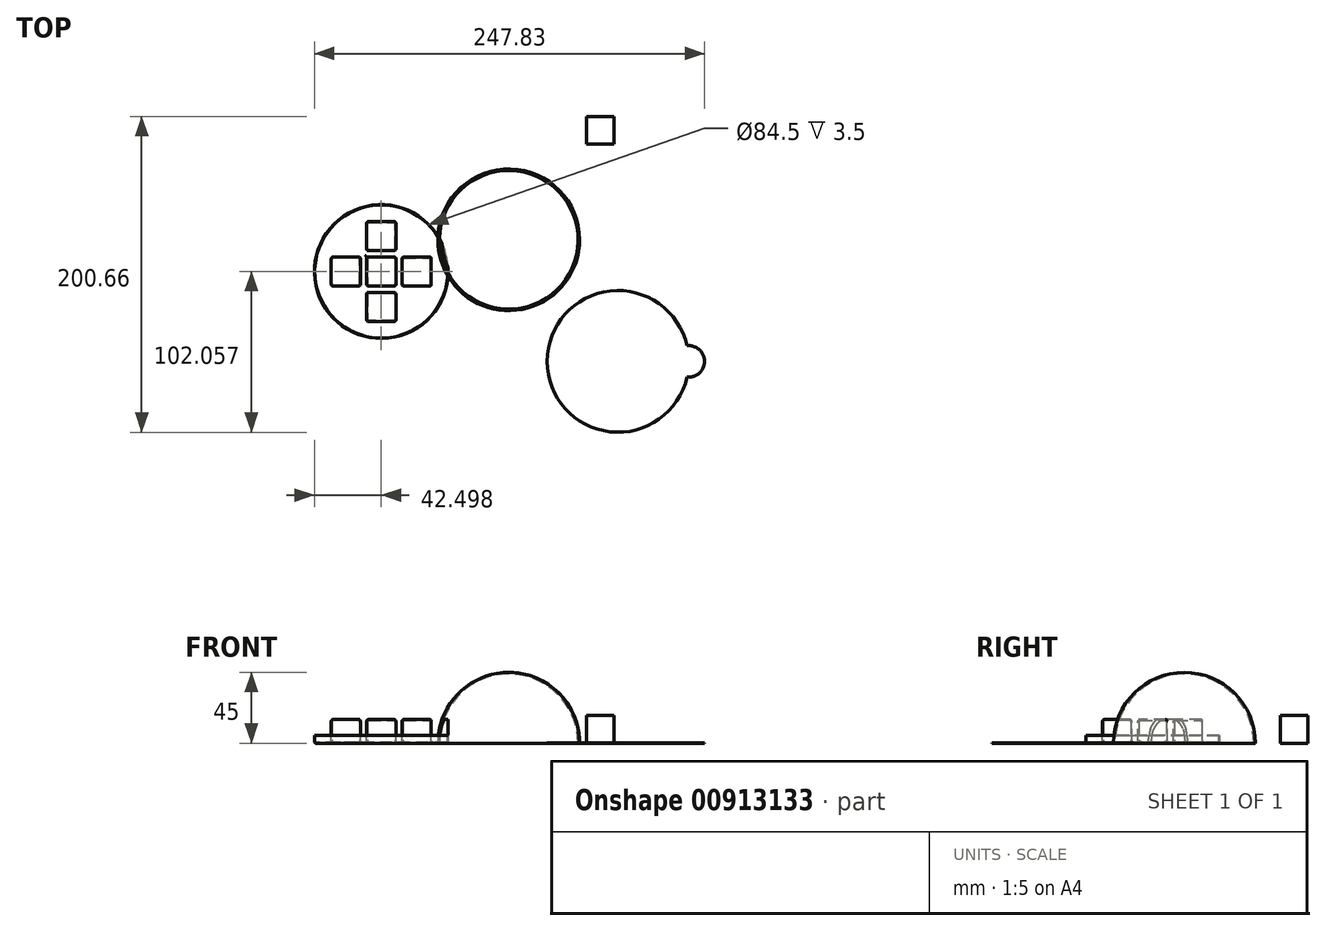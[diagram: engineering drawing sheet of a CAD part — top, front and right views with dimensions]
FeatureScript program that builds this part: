
annotation { "Feature Type Name" : "Feature", "Feature Type Description" : "" }
export const myFeature = defineFeature(function(context is Context, id is Id, definition is map)
    precondition{}
    {
        {
            var Q0;
            Q0=qCreatedBy(makeId("Top.planeOp"),FACE);
            var sketch = newSketch(context, id + "F0", { "sketchPlane" : qUnion([Q0])});
            skCircle(sketch, "E0", {"center": v(0, 0) * mm, "radius": 45 * mm});
            skSolve(sketch);
        }
        {
            var Q0;
            Q0 = qSketchRegion(id + "F0", true);
            extrude(context, id + "F1", {"entities" : qUnion([Q0]), "depth" : 45 * mm, "offsetDistance" : 25 * mm});
        }
        {
            var Q0;
            Q0=makeQuery(id+"F1.opExtrude","CAP_EDGE",EDGE,{"disambiguationData":[OSD([sQuery(id+"F0.wireOp",EDGE,"E0")])],"isStart":false});
            fillet(context, id + "F2", {"entities" : qUnion([Q0]), "radius" : 45 * mm, "tangentPropagation" : true, "allowEdgeOverflow" : false});
        }
        {
            var Q0;
            Q0=makeQuery(id+"F1.opExtrude","CAP_FACE",FACE,{"disambiguationData":[OSD([sQuery(id+"F0.wireOp",EDGE,"E0")])],"isStart":true});
            shell(context, id + "F3", {"entities" : qUnion([Q0]), "thickness" : 1 * mm});
        }
        {
            var Q0;
            Q0=qCreatedBy(makeId("Top.planeOp"),FACE);
            var sketch = newSketch(context, id + "F4", { "sketchPlane" : qUnion([Q0])});
            skCircle(sketch, "E1", {"center": v(-80.96, -20.16) * mm, "radius": 42.5 * mm});
            skSolve(sketch);
        }
        {
            var Q0;
            Q0 = qSketchRegion(id + "F4", true);
            extrude(context, id + "F5", {"entities" : qUnion([Q0]), "depth" : 15 * mm, "offsetDistance" : 25 * mm});
        }
        {
            var Q0;
            Q0=makeQuery(id+"F5.opExtrude","CAP_FACE",FACE,{"disambiguationData":[OSD([sQuery(id+"F4.wireOp",EDGE,"E1")])],"isStart":true});
            var sketch = newSketch(context, id + "F6", { "sketchPlane" : qUnion([Q0])});
            skLineSegment(sketch, "E2.bottom", {"start": v(-72.21, 11.41) * mm, "end": v(-89.71, 11.41) * mm});
            skLineSegment(sketch, "E2.left", {"start": v(-72.21, 11.41) * mm, "end": v(-72.21, 28.91) * mm});
            skLineSegment(sketch, "E2.right", {"start": v(-89.71, 11.41) * mm, "end": v(-89.71, 28.91) * mm});
            skPoint(sketch, "E3.endSnap0", {"position": v(-72.21, 20.16) * mm});
            skLineSegment(sketch, "E4.bottom", {"start": v(-72.21, 33.91) * mm, "end": v(-89.71, 33.91) * mm});
            skLineSegment(sketch, "E4.top", {"start": v(-72.21, 51.41) * mm, "end": v(-89.71, 51.41) * mm});
            skLineSegment(sketch, "E4.left", {"start": v(-72.21, 33.91) * mm, "end": v(-72.21, 51.41) * mm});
            skLineSegment(sketch, "E4.right", {"start": v(-89.71, 33.91) * mm, "end": v(-89.71, 51.41) * mm});
            skLineSegment(sketch, "E5.bottom", {"start": v(-89.71, 6.41) * mm, "end": v(-72.21, 6.41) * mm});
            skLineSegment(sketch, "E5.top", {"start": v(-89.71, -11.09) * mm, "end": v(-72.21, -11.09) * mm});
            skLineSegment(sketch, "E5.left", {"start": v(-89.71, 6.41) * mm, "end": v(-89.71, -11.09) * mm});
            skLineSegment(sketch, "E5.right", {"start": v(-72.21, 6.41) * mm, "end": v(-72.21, -11.09) * mm});
            skLineSegment(sketch, "E6.bottom", {"start": v(-94.71, 28.91) * mm, "end": v(-112.21, 28.91) * mm});
            skLineSegment(sketch, "E6.top", {"start": v(-94.71, 11.41) * mm, "end": v(-112.21, 11.41) * mm});
            skLineSegment(sketch, "E6.left", {"start": v(-94.71, 28.91) * mm, "end": v(-94.71, 11.41) * mm});
            skLineSegment(sketch, "E6.right", {"start": v(-112.21, 28.91) * mm, "end": v(-112.21, 11.41) * mm});
            skLineSegment(sketch, "E7.bottom", {"start": v(-67.21, 28.91) * mm, "end": v(-49.71, 28.91) * mm});
            skLineSegment(sketch, "E7.top", {"start": v(-67.21, 11.41) * mm, "end": v(-49.71, 11.41) * mm});
            skLineSegment(sketch, "E7.left", {"start": v(-67.21, 28.91) * mm, "end": v(-67.21, 11.41) * mm});
            skLineSegment(sketch, "E7.right", {"start": v(-49.71, 28.91) * mm, "end": v(-49.71, 11.41) * mm});
            skLineSegment(sketch, "E8", {"start": v(-89.71, 28.91) * mm, "end": v(-72.21, 28.91) * mm});
            skLineSegment(sketch, "E9", {"start": v(-89.71, 20.16) * mm, "end": v(-80.96, 20.16) * mm});
            skLineSegment(sketch, "E10", {"start": v(-80.96, 28.91) * mm, "end": v(-80.96, 20.16) * mm});
            skSolve(sketch);
        }
        {
            var Q0;
            Q0=qCreatedBy(makeId("Top.planeOp"),FACE);
            var sketch = newSketch(context, id + "F7", { "sketchPlane" : qUnion([Q0])});
            skLineSegment(sketch, "E11.bottom", {"start": v(66.92, 60.94) * mm, "end": v(49.42, 60.94) * mm});
            skLineSegment(sketch, "E11.top", {"start": v(66.92, 78.44) * mm, "end": v(49.42, 78.44) * mm});
            skLineSegment(sketch, "E11.left", {"start": v(66.92, 60.94) * mm, "end": v(66.92, 78.44) * mm});
            skLineSegment(sketch, "E11.right", {"start": v(49.42, 60.94) * mm, "end": v(49.42, 78.44) * mm});
            skSolve(sketch);
        }
        {
            var Q0;
            Q0 = qSketchRegion(id + "F7", true);
            extrude(context, id + "F8", {"entities" : qUnion([Q0]), "depth" : 17.5 * mm, "offsetDistance" : 25 * mm});
        }
        {
            var Q0;
            Q0 = qSketchRegion(id + "F6", true);
            extrude(context, id + "F9", {"entities" : qUnion([Q0]), "operationType" : NewBodyOperationType.REMOVE, "oppositeDirection" : true, "depth" : 14.5 * mm, "offsetDistance" : 25 * mm});
        }
        {
            var Q0;
            Q0=makeQuery(id+"F5.opExtrude","CAP_FACE",FACE,{"disambiguationData":[OSD([sQuery(id+"F4.wireOp",EDGE,"E1")])],"isStart":false});
            var sketch = newSketch(context, id + "F10", { "sketchPlane" : qUnion([Q0])});
            skCircle(sketch, "E12", {"center": v(-80.96, -20.16) * mm, "radius": 42.25 * mm});
            skLineSegment(sketch, "E13.bottom", {"start": v(-90.21, 11.59) * mm, "end": v(-71.71, 11.59) * mm});
            skLineSegment(sketch, "E13.top", {"start": v(-90.21, -6.91) * mm, "end": v(-71.71, -6.91) * mm});
            skLineSegment(sketch, "E13.left", {"start": v(-90.21, 11.59) * mm, "end": v(-90.21, -6.91) * mm});
            skLineSegment(sketch, "E13.right", {"start": v(-71.71, 11.59) * mm, "end": v(-71.71, -6.91) * mm});
            skLineSegment(sketch, "E14.bottom", {"start": v(-90.21, -10.91) * mm, "end": v(-71.71, -10.91) * mm});
            skLineSegment(sketch, "E14.top", {"start": v(-90.21, -29.41) * mm, "end": v(-71.71, -29.41) * mm});
            skLineSegment(sketch, "E14.left", {"start": v(-90.21, -10.91) * mm, "end": v(-90.21, -29.41) * mm});
            skLineSegment(sketch, "E14.right", {"start": v(-71.71, -10.91) * mm, "end": v(-71.71, -29.41) * mm});
            skLineSegment(sketch, "E15.bottom", {"start": v(-94.21, -10.91) * mm, "end": v(-112.71, -10.91) * mm});
            skLineSegment(sketch, "E15.top", {"start": v(-94.21, -29.41) * mm, "end": v(-112.71, -29.41) * mm});
            skLineSegment(sketch, "E15.left", {"start": v(-94.21, -10.91) * mm, "end": v(-94.21, -29.41) * mm});
            skLineSegment(sketch, "E15.right", {"start": v(-112.71, -10.91) * mm, "end": v(-112.71, -29.41) * mm});
            skLineSegment(sketch, "E16.bottom", {"start": v(-67.71, -10.91) * mm, "end": v(-49.21, -10.91) * mm});
            skLineSegment(sketch, "E16.top", {"start": v(-67.71, -29.41) * mm, "end": v(-49.21, -29.41) * mm});
            skLineSegment(sketch, "E16.left", {"start": v(-67.71, -10.91) * mm, "end": v(-67.71, -29.41) * mm});
            skLineSegment(sketch, "E16.right", {"start": v(-49.21, -10.91) * mm, "end": v(-49.21, -29.41) * mm});
            skLineSegment(sketch, "E17.bottom", {"start": v(-90.21, -33.41) * mm, "end": v(-71.71, -33.41) * mm});
            skLineSegment(sketch, "E17.top", {"start": v(-90.21, -51.91) * mm, "end": v(-71.71, -51.91) * mm});
            skLineSegment(sketch, "E17.left", {"start": v(-90.21, -33.41) * mm, "end": v(-90.21, -51.91) * mm});
            skLineSegment(sketch, "E17.right", {"start": v(-71.71, -33.41) * mm, "end": v(-71.71, -51.91) * mm});
            skSolve(sketch);
        }
        {
            var Q0;
            Q0 = qSketchRegion(id + "F10", true);
            extrude(context, id + "F11", {"entities" : qUnion([Q0]), "operationType" : NewBodyOperationType.REMOVE, "oppositeDirection" : true, "depth" : 14.5 * mm, "offsetDistance" : 25 * mm});
        }
        {
            var Q0;
            {var subQ0=sQuery(id+"F4.wireOp",EDGE,"E1");Q0=makeQuery(id+"F11.boolean.opBoolean","SPLIT",FACE,{"disambiguationData":[TD([makeQuery(id+"F5.opExtrude","SWEPT_FACE",FACE,{"disambiguationData":[OSD([subQ0])]})])],"derivedFrom":makeQuery(id+"F5.opExtrude","CAP_FACE",FACE,{"disambiguationData":[OSD([subQ0])],"isStart":false})});}
            var sketch = newSketch(context, id + "F12", { "sketchPlane" : qUnion([Q0])});
            skCircle(sketch, "E18", {"center": v(-80.96, -20.16) * mm, "radius": 42.5 * mm});
            skCircle(sketch, "E19", {"center": v(-80.96, -20.16) * mm, "radius": 42.25 * mm});
            skSolve(sketch);
        }
        {
            var Q0;
            Q0 = qSketchRegion(id + "F12", true);
            extrude(context, id + "F13", {"entities" : qUnion([Q0]), "operationType" : NewBodyOperationType.REMOVE, "oppositeDirection" : true, "depth" : 10 * mm, "offsetDistance" : 25 * mm});
        }
        {
            var Q0;
            Q0=makeQuery(id+"F13.boolean.opBoolean","COPY",EDGE,{"derivedFrom":makeQuery(id+"F13.opExtrude","CAP_EDGE",EDGE,{"disambiguationData":[OSD([sQuery(id+"F12.wireOp",EDGE,"E18")])],"isStart":false})});
            fillet(context, id + "F14", {"entities" : qUnion([Q0]), "radius" : 30 * mm, "tangentPropagation" : true, "allowEdgeOverflow" : false});
        }
        {
            var Q0;
            Q0=makeQuery(id+"F11.boolean.opBoolean","COPY",EDGE,{"derivedFrom":makeQuery(id+"F11.opExtrude","CAP_EDGE",EDGE,{"disambiguationData":[OSD([sQuery(id+"F10.wireOp",EDGE,"E15.bottom")])],"isStart":true})});
            var Q1;
            Q1=makeQuery(id+"F11.boolean.opBoolean","COPY",EDGE,{"derivedFrom":makeQuery(id+"F11.opExtrude","CAP_EDGE",EDGE,{"disambiguationData":[OSD([sQuery(id+"F10.wireOp",EDGE,"E15.right")])],"isStart":true})});
            var Q2;
            Q2=makeQuery(id+"F11.boolean.opBoolean","COPY",EDGE,{"derivedFrom":makeQuery(id+"F11.opExtrude","CAP_EDGE",EDGE,{"disambiguationData":[OSD([sQuery(id+"F10.wireOp",EDGE,"E15.top")])],"isStart":true})});
            var Q3;
            Q3=makeQuery(id+"F11.boolean.opBoolean","COPY",EDGE,{"derivedFrom":makeQuery(id+"F11.opExtrude","CAP_EDGE",EDGE,{"disambiguationData":[OSD([sQuery(id+"F10.wireOp",EDGE,"E15.left")])],"isStart":true})});
            var Q4;
            Q4=makeQuery(id+"F11.boolean.opBoolean","COPY",EDGE,{"derivedFrom":makeQuery(id+"F11.opExtrude","CAP_EDGE",EDGE,{"disambiguationData":[OSD([sQuery(id+"F10.wireOp",EDGE,"E14.left")])],"isStart":true})});
            var Q5;
            Q5=makeQuery(id+"F11.boolean.opBoolean","COPY",EDGE,{"derivedFrom":makeQuery(id+"F11.opExtrude","CAP_EDGE",EDGE,{"disambiguationData":[OSD([sQuery(id+"F10.wireOp",EDGE,"E14.top")])],"isStart":true})});
            var Q6;
            Q6=makeQuery(id+"F11.boolean.opBoolean","COPY",EDGE,{"derivedFrom":makeQuery(id+"F11.opExtrude","CAP_EDGE",EDGE,{"disambiguationData":[OSD([sQuery(id+"F10.wireOp",EDGE,"E14.right")])],"isStart":true})});
            var Q7;
            Q7=makeQuery(id+"F11.boolean.opBoolean","COPY",EDGE,{"derivedFrom":makeQuery(id+"F11.opExtrude","CAP_EDGE",EDGE,{"disambiguationData":[OSD([sQuery(id+"F10.wireOp",EDGE,"E14.bottom")])],"isStart":true})});
            var Q8;
            Q8=makeQuery(id+"F11.boolean.opBoolean","COPY",EDGE,{"derivedFrom":makeQuery(id+"F11.opExtrude","CAP_EDGE",EDGE,{"disambiguationData":[OSD([sQuery(id+"F10.wireOp",EDGE,"E13.top")])],"isStart":true})});
            var Q9;
            Q9=makeQuery(id+"F11.boolean.opBoolean","COPY",EDGE,{"derivedFrom":makeQuery(id+"F11.opExtrude","CAP_EDGE",EDGE,{"disambiguationData":[OSD([sQuery(id+"F10.wireOp",EDGE,"E13.left")])],"isStart":true})});
            var Q10;
            Q10=makeQuery(id+"F11.boolean.opBoolean","COPY",EDGE,{"derivedFrom":makeQuery(id+"F11.opExtrude","CAP_EDGE",EDGE,{"disambiguationData":[OSD([sQuery(id+"F10.wireOp",EDGE,"E13.bottom")])],"isStart":true})});
            var Q11;
            Q11=makeQuery(id+"F11.boolean.opBoolean","COPY",EDGE,{"derivedFrom":makeQuery(id+"F11.opExtrude","CAP_EDGE",EDGE,{"disambiguationData":[OSD([sQuery(id+"F10.wireOp",EDGE,"E13.right")])],"isStart":true})});
            var Q12;
            Q12=makeQuery(id+"F11.boolean.opBoolean","COPY",EDGE,{"derivedFrom":makeQuery(id+"F11.opExtrude","CAP_EDGE",EDGE,{"disambiguationData":[OSD([sQuery(id+"F10.wireOp",EDGE,"E16.bottom")])],"isStart":true})});
            var Q13;
            Q13=makeQuery(id+"F11.boolean.opBoolean","COPY",EDGE,{"derivedFrom":makeQuery(id+"F11.opExtrude","CAP_EDGE",EDGE,{"disambiguationData":[OSD([sQuery(id+"F10.wireOp",EDGE,"E16.left")])],"isStart":true})});
            var Q14;
            Q14=makeQuery(id+"F11.boolean.opBoolean","COPY",EDGE,{"derivedFrom":makeQuery(id+"F11.opExtrude","CAP_EDGE",EDGE,{"disambiguationData":[OSD([sQuery(id+"F10.wireOp",EDGE,"E16.top")])],"isStart":true})});
            var Q15;
            Q15=makeQuery(id+"F11.boolean.opBoolean","COPY",EDGE,{"derivedFrom":makeQuery(id+"F11.opExtrude","CAP_EDGE",EDGE,{"disambiguationData":[OSD([sQuery(id+"F10.wireOp",EDGE,"E16.right")])],"isStart":true})});
            var Q16;
            Q16=makeQuery(id+"F11.boolean.opBoolean","COPY",EDGE,{"derivedFrom":makeQuery(id+"F11.opExtrude","CAP_EDGE",EDGE,{"disambiguationData":[OSD([sQuery(id+"F10.wireOp",EDGE,"E17.top")])],"isStart":true})});
            var Q17;
            Q17=makeQuery(id+"F11.boolean.opBoolean","COPY",EDGE,{"derivedFrom":makeQuery(id+"F11.opExtrude","CAP_EDGE",EDGE,{"disambiguationData":[OSD([sQuery(id+"F10.wireOp",EDGE,"E17.left")])],"isStart":true})});
            var Q18;
            Q18=makeQuery(id+"F11.boolean.opBoolean","COPY",EDGE,{"derivedFrom":makeQuery(id+"F11.opExtrude","CAP_EDGE",EDGE,{"disambiguationData":[OSD([sQuery(id+"F10.wireOp",EDGE,"E17.bottom")])],"isStart":true})});
            var Q19;
            Q19=makeQuery(id+"F11.boolean.opBoolean","COPY",EDGE,{"derivedFrom":makeQuery(id+"F11.opExtrude","CAP_EDGE",EDGE,{"disambiguationData":[OSD([sQuery(id+"F10.wireOp",EDGE,"E17.right")])],"isStart":true})});
            var Q20;
            Q20=makeQuery(id+"F11.boolean.opBoolean","COPY",EDGE,{"derivedFrom":makeQuery(id+"F11.opExtrude","SWEPT_EDGE",EDGE,{"disambiguationData":[OSD([sQuery(id+"F10.wireOp",EDGE,"E15.top"),sQuery(id+"F10.wireOp",EDGE,"E15.right")])]})});
            var Q21;
            Q21=makeQuery(id+"F11.boolean.opBoolean","COPY",EDGE,{"derivedFrom":makeQuery(id+"F11.opExtrude","SWEPT_EDGE",EDGE,{"disambiguationData":[OSD([sQuery(id+"F10.wireOp",EDGE,"E15.top"),sQuery(id+"F10.wireOp",EDGE,"E15.left")])]})});
            var Q22;
            Q22=makeQuery(id+"F11.boolean.opBoolean","COPY",EDGE,{"derivedFrom":makeQuery(id+"F11.opExtrude","CAP_EDGE",EDGE,{"disambiguationData":[OSD([sQuery(id+"F10.wireOp",EDGE,"E15.top")])],"isStart":false})});
            var Q23;
            Q23=makeQuery(id+"F11.boolean.opBoolean","COPY",EDGE,{"derivedFrom":makeQuery(id+"F11.opExtrude","CAP_EDGE",EDGE,{"disambiguationData":[OSD([sQuery(id+"F10.wireOp",EDGE,"E14.left")])],"isStart":false})});
            var Q24;
            Q24=makeQuery(id+"F11.boolean.opBoolean","COPY",EDGE,{"derivedFrom":makeQuery(id+"F11.opExtrude","CAP_EDGE",EDGE,{"disambiguationData":[OSD([sQuery(id+"F10.wireOp",EDGE,"E17.left")])],"isStart":false})});
            var Q25;
            Q25=makeQuery(id+"F11.boolean.opBoolean","COPY",EDGE,{"derivedFrom":makeQuery(id+"F11.opExtrude","CAP_EDGE",EDGE,{"disambiguationData":[OSD([sQuery(id+"F10.wireOp",EDGE,"E16.top")])],"isStart":false})});
            var Q26;
            Q26=makeQuery(id+"F11.boolean.opBoolean","COPY",EDGE,{"derivedFrom":makeQuery(id+"F11.opExtrude","CAP_EDGE",EDGE,{"disambiguationData":[OSD([sQuery(id+"F10.wireOp",EDGE,"E13.bottom")])],"isStart":false})});
            var Q27;
            Q27=makeQuery(id+"F11.boolean.opBoolean","COPY",EDGE,{"derivedFrom":makeQuery(id+"F11.opExtrude","CAP_EDGE",EDGE,{"disambiguationData":[OSD([sQuery(id+"F10.wireOp",EDGE,"E15.bottom")])],"isStart":false})});
            var Q28;
            Q28=makeQuery(id+"F11.boolean.opBoolean","COPY",EDGE,{"derivedFrom":makeQuery(id+"F11.opExtrude","CAP_EDGE",EDGE,{"disambiguationData":[OSD([sQuery(id+"F10.wireOp",EDGE,"E16.bottom")])],"isStart":false})});
            var Q29;
            Q29=makeQuery(id+"F11.boolean.opBoolean","COPY",EDGE,{"derivedFrom":makeQuery(id+"F11.opExtrude","SWEPT_EDGE",EDGE,{"disambiguationData":[OSD([sQuery(id+"F10.wireOp",EDGE,"E16.bottom"),sQuery(id+"F10.wireOp",EDGE,"E16.left")])]})});
            var Q30;
            Q30=makeQuery(id+"F11.boolean.opBoolean","COPY",EDGE,{"derivedFrom":makeQuery(id+"F11.opExtrude","CAP_EDGE",EDGE,{"disambiguationData":[OSD([sQuery(id+"F10.wireOp",EDGE,"E14.bottom")])],"isStart":false})});
            var Q31;
            Q31=makeQuery(id+"F11.boolean.opBoolean","COPY",EDGE,{"derivedFrom":makeQuery(id+"F11.opExtrude","CAP_EDGE",EDGE,{"disambiguationData":[OSD([sQuery(id+"F10.wireOp",EDGE,"E13.right")])],"isStart":false})});
            var Q32;
            Q32=makeQuery(id+"F11.boolean.opBoolean","COPY",EDGE,{"derivedFrom":makeQuery(id+"F11.opExtrude","CAP_EDGE",EDGE,{"disambiguationData":[OSD([sQuery(id+"F10.wireOp",EDGE,"E13.top")])],"isStart":false})});
            var Q33;
            Q33=makeQuery(id+"F11.boolean.opBoolean","COPY",EDGE,{"derivedFrom":makeQuery(id+"F11.opExtrude","CAP_EDGE",EDGE,{"disambiguationData":[OSD([sQuery(id+"F10.wireOp",EDGE,"E13.left")])],"isStart":false})});
            var Q34;
            Q34=makeQuery(id+"F11.boolean.opBoolean","COPY",EDGE,{"derivedFrom":makeQuery(id+"F11.opExtrude","CAP_EDGE",EDGE,{"disambiguationData":[OSD([sQuery(id+"F10.wireOp",EDGE,"E14.top")])],"isStart":false})});
            var Q35;
            Q35=makeQuery(id+"F11.boolean.opBoolean","COPY",EDGE,{"derivedFrom":makeQuery(id+"F11.opExtrude","CAP_EDGE",EDGE,{"disambiguationData":[OSD([sQuery(id+"F10.wireOp",EDGE,"E17.top")])],"isStart":false})});
            var Q36;
            Q36=makeQuery(id+"F11.boolean.opBoolean","COPY",EDGE,{"derivedFrom":makeQuery(id+"F11.opExtrude","CAP_EDGE",EDGE,{"disambiguationData":[OSD([sQuery(id+"F10.wireOp",EDGE,"E17.bottom")])],"isStart":false})});
            var Q37;
            Q37=makeQuery(id+"F11.boolean.opBoolean","COPY",EDGE,{"derivedFrom":makeQuery(id+"F11.opExtrude","SWEPT_EDGE",EDGE,{"disambiguationData":[OSD([sQuery(id+"F10.wireOp",EDGE,"E13.bottom"),sQuery(id+"F10.wireOp",EDGE,"E13.left")])]})});
            var Q38;
            Q38=makeQuery(id+"F11.boolean.opBoolean","COPY",EDGE,{"derivedFrom":makeQuery(id+"F11.opExtrude","SWEPT_EDGE",EDGE,{"disambiguationData":[OSD([sQuery(id+"F10.wireOp",EDGE,"E13.top"),sQuery(id+"F10.wireOp",EDGE,"E13.left")])]})});
            var Q39;
            Q39=makeQuery(id+"F11.boolean.opBoolean","COPY",EDGE,{"derivedFrom":makeQuery(id+"F11.opExtrude","SWEPT_EDGE",EDGE,{"disambiguationData":[OSD([sQuery(id+"F10.wireOp",EDGE,"E15.bottom"),sQuery(id+"F10.wireOp",EDGE,"E15.left")])]})});
            var Q40;
            Q40=makeQuery(id+"F11.boolean.opBoolean","COPY",EDGE,{"derivedFrom":makeQuery(id+"F11.opExtrude","SWEPT_EDGE",EDGE,{"disambiguationData":[OSD([sQuery(id+"F10.wireOp",EDGE,"E15.bottom"),sQuery(id+"F10.wireOp",EDGE,"E15.right")])]})});
            var Q41;
            Q41=makeQuery(id+"F11.boolean.opBoolean","COPY",EDGE,{"derivedFrom":makeQuery(id+"F11.opExtrude","SWEPT_EDGE",EDGE,{"disambiguationData":[OSD([sQuery(id+"F10.wireOp",EDGE,"E17.bottom"),sQuery(id+"F10.wireOp",EDGE,"E17.left")])]})});
            var Q42;
            Q42=makeQuery(id+"F11.boolean.opBoolean","COPY",EDGE,{"derivedFrom":makeQuery(id+"F11.opExtrude","SWEPT_EDGE",EDGE,{"disambiguationData":[OSD([sQuery(id+"F10.wireOp",EDGE,"E14.top"),sQuery(id+"F10.wireOp",EDGE,"E14.left")])]})});
            var Q43;
            Q43=makeQuery(id+"F11.boolean.opBoolean","COPY",EDGE,{"derivedFrom":makeQuery(id+"F11.opExtrude","SWEPT_EDGE",EDGE,{"disambiguationData":[OSD([sQuery(id+"F10.wireOp",EDGE,"E17.top"),sQuery(id+"F10.wireOp",EDGE,"E17.left")])]})});
            var Q44;
            Q44=makeQuery(id+"F11.boolean.opBoolean","COPY",EDGE,{"derivedFrom":makeQuery(id+"F11.opExtrude","SWEPT_EDGE",EDGE,{"disambiguationData":[OSD([sQuery(id+"F10.wireOp",EDGE,"E17.top"),sQuery(id+"F10.wireOp",EDGE,"E17.right")])]})});
            var Q45;
            Q45=makeQuery(id+"F11.boolean.opBoolean","COPY",EDGE,{"derivedFrom":makeQuery(id+"F11.opExtrude","CAP_EDGE",EDGE,{"disambiguationData":[OSD([sQuery(id+"F10.wireOp",EDGE,"E17.right")])],"isStart":false})});
            var Q46;
            Q46=makeQuery(id+"F11.boolean.opBoolean","COPY",EDGE,{"derivedFrom":makeQuery(id+"F11.opExtrude","SWEPT_EDGE",EDGE,{"disambiguationData":[OSD([sQuery(id+"F10.wireOp",EDGE,"E17.bottom"),sQuery(id+"F10.wireOp",EDGE,"E17.right")])]})});
            var Q47;
            Q47=makeQuery(id+"F11.boolean.opBoolean","COPY",EDGE,{"derivedFrom":makeQuery(id+"F11.opExtrude","SWEPT_EDGE",EDGE,{"disambiguationData":[OSD([sQuery(id+"F10.wireOp",EDGE,"E14.top"),sQuery(id+"F10.wireOp",EDGE,"E14.right")])]})});
            var Q48;
            Q48=makeQuery(id+"F11.boolean.opBoolean","COPY",EDGE,{"derivedFrom":makeQuery(id+"F11.opExtrude","CAP_EDGE",EDGE,{"disambiguationData":[OSD([sQuery(id+"F10.wireOp",EDGE,"E14.right")])],"isStart":false})});
            var Q49;
            Q49=makeQuery(id+"F11.boolean.opBoolean","COPY",EDGE,{"derivedFrom":makeQuery(id+"F11.opExtrude","SWEPT_EDGE",EDGE,{"disambiguationData":[OSD([sQuery(id+"F10.wireOp",EDGE,"E13.top"),sQuery(id+"F10.wireOp",EDGE,"E13.right")])]})});
            var Q50;
            Q50=makeQuery(id+"F11.boolean.opBoolean","COPY",EDGE,{"derivedFrom":makeQuery(id+"F11.opExtrude","SWEPT_EDGE",EDGE,{"disambiguationData":[OSD([sQuery(id+"F10.wireOp",EDGE,"E14.bottom"),sQuery(id+"F10.wireOp",EDGE,"E14.right")])]})});
            var Q51;
            Q51=makeQuery(id+"F11.boolean.opBoolean","COPY",EDGE,{"derivedFrom":makeQuery(id+"F11.opExtrude","SWEPT_EDGE",EDGE,{"disambiguationData":[OSD([sQuery(id+"F10.wireOp",EDGE,"E16.top"),sQuery(id+"F10.wireOp",EDGE,"E16.right")])]})});
            var Q52;
            Q52=makeQuery(id+"F11.boolean.opBoolean","COPY",EDGE,{"derivedFrom":makeQuery(id+"F11.opExtrude","SWEPT_EDGE",EDGE,{"disambiguationData":[OSD([sQuery(id+"F10.wireOp",EDGE,"E13.bottom"),sQuery(id+"F10.wireOp",EDGE,"E13.right")])]})});
            var Q53;
            Q53=makeQuery(id+"F11.boolean.opBoolean","COPY",EDGE,{"derivedFrom":makeQuery(id+"F11.opExtrude","SWEPT_EDGE",EDGE,{"disambiguationData":[OSD([sQuery(id+"F10.wireOp",EDGE,"E16.top"),sQuery(id+"F10.wireOp",EDGE,"E16.left")])]})});
            var Q54;
            Q54=makeQuery(id+"F11.boolean.opBoolean","COPY",EDGE,{"derivedFrom":makeQuery(id+"F11.opExtrude","SWEPT_EDGE",EDGE,{"disambiguationData":[OSD([sQuery(id+"F10.wireOp",EDGE,"E16.bottom"),sQuery(id+"F10.wireOp",EDGE,"E16.right")])]})});
            var Q55;
            Q55=makeQuery(id+"F11.boolean.opBoolean","COPY",EDGE,{"derivedFrom":makeQuery(id+"F11.opExtrude","CAP_EDGE",EDGE,{"disambiguationData":[OSD([sQuery(id+"F10.wireOp",EDGE,"E12")])],"isStart":false})});
            var Q56;
            Q56=makeQuery(id+"F9.boolean.opBoolean","COPY",EDGE,{"derivedFrom":makeQuery(id+"F9.opExtrude","CAP_EDGE",EDGE,{"disambiguationData":[OSD([sQuery(id+"F6.wireOp",EDGE,"E4.bottom")])],"isStart":true})});
            fillet(context, id + "F15", {"entities" : qUnion([Q0, Q1, Q2, Q3, Q4, Q5, Q6, Q7, Q8, Q9, Q10, Q11, Q12, Q13, Q14, Q15, Q16, Q17, Q18, Q19, Q20, Q21, Q22, Q23, Q24, Q25, Q26, Q27, Q28, Q29, Q30, Q31, Q32, Q33, Q34, Q35, Q36, Q37, Q38, Q39, Q40, Q41, Q42, Q43, Q44, Q45, Q46, Q47, Q48, Q49, Q50, Q51, Q52, Q53, Q54, Q55, Q56]), "radius" : 1 * mm, "tangentPropagation" : true, "allowEdgeOverflow" : false});
        }
        {
            var Q0;
            Q0=makeQuery(id+"F9.boolean.opBoolean","COPY",EDGE,{"derivedFrom":makeQuery(id+"F9.opExtrude","CAP_EDGE",EDGE,{"disambiguationData":[OSD([sQuery(id+"F6.wireOp",EDGE,"E4.right")])],"isStart":true})});
            var Q1;
            Q1=makeQuery(id+"F9.boolean.opBoolean","COPY",EDGE,{"derivedFrom":makeQuery(id+"F9.opExtrude","CAP_EDGE",EDGE,{"disambiguationData":[OSD([sQuery(id+"F6.wireOp",EDGE,"E4.top")])],"isStart":true})});
            var Q2;
            Q2=makeQuery(id+"F9.boolean.opBoolean","COPY",EDGE,{"derivedFrom":makeQuery(id+"F9.opExtrude","CAP_EDGE",EDGE,{"disambiguationData":[OSD([sQuery(id+"F6.wireOp",EDGE,"E4.left")])],"isStart":true})});
            var Q3;
            Q3=makeQuery(id+"F9.boolean.opBoolean","COPY",EDGE,{"derivedFrom":makeQuery(id+"F9.opExtrude","CAP_EDGE",EDGE,{"disambiguationData":[OSD([sQuery(id+"F6.wireOp",EDGE,"E7.bottom")])],"isStart":true})});
            var Q4;
            Q4=makeQuery(id+"F9.boolean.opBoolean","COPY",EDGE,{"derivedFrom":makeQuery(id+"F9.opExtrude","CAP_EDGE",EDGE,{"disambiguationData":[OSD([sQuery(id+"F6.wireOp",EDGE,"E7.left")])],"isStart":true})});
            var Q5;
            Q5=makeQuery(id+"F9.boolean.opBoolean","COPY",EDGE,{"derivedFrom":makeQuery(id+"F9.opExtrude","CAP_EDGE",EDGE,{"disambiguationData":[OSD([sQuery(id+"F6.wireOp",EDGE,"E7.top")])],"isStart":true})});
            var Q6;
            Q6=makeQuery(id+"F9.boolean.opBoolean","COPY",EDGE,{"derivedFrom":makeQuery(id+"F9.opExtrude","CAP_EDGE",EDGE,{"disambiguationData":[OSD([sQuery(id+"F6.wireOp",EDGE,"E7.right")])],"isStart":true})});
            var Q7;
            Q7=makeQuery(id+"F9.boolean.opBoolean","COPY",EDGE,{"derivedFrom":makeQuery(id+"F9.opExtrude","CAP_EDGE",EDGE,{"disambiguationData":[OSD([sQuery(id+"F6.wireOp",EDGE,"E2.left")])],"isStart":true})});
            var Q8;
            Q8=makeQuery(id+"F9.boolean.opBoolean","COPY",EDGE,{"derivedFrom":makeQuery(id+"F9.opExtrude","CAP_EDGE",EDGE,{"disambiguationData":[OSD([sQuery(id+"F6.wireOp",EDGE,"E8")])],"isStart":true})});
            var Q9;
            Q9=makeQuery(id+"F9.boolean.opBoolean","COPY",EDGE,{"derivedFrom":makeQuery(id+"F9.opExtrude","CAP_EDGE",EDGE,{"disambiguationData":[OSD([sQuery(id+"F6.wireOp",EDGE,"E2.right")])],"isStart":true})});
            var Q10;
            Q10=makeQuery(id+"F9.boolean.opBoolean","COPY",EDGE,{"derivedFrom":makeQuery(id+"F9.opExtrude","CAP_EDGE",EDGE,{"disambiguationData":[OSD([sQuery(id+"F6.wireOp",EDGE,"E2.bottom")])],"isStart":true})});
            var Q11;
            Q11=makeQuery(id+"F9.boolean.opBoolean","COPY",EDGE,{"derivedFrom":makeQuery(id+"F9.opExtrude","CAP_EDGE",EDGE,{"disambiguationData":[OSD([sQuery(id+"F6.wireOp",EDGE,"E6.bottom")])],"isStart":true})});
            var Q12;
            Q12=makeQuery(id+"F9.boolean.opBoolean","COPY",EDGE,{"derivedFrom":makeQuery(id+"F9.opExtrude","CAP_EDGE",EDGE,{"disambiguationData":[OSD([sQuery(id+"F6.wireOp",EDGE,"E6.right")])],"isStart":true})});
            var Q13;
            Q13=makeQuery(id+"F9.boolean.opBoolean","COPY",EDGE,{"derivedFrom":makeQuery(id+"F9.opExtrude","CAP_EDGE",EDGE,{"disambiguationData":[OSD([sQuery(id+"F6.wireOp",EDGE,"E6.top")])],"isStart":true})});
            var Q14;
            Q14=makeQuery(id+"F9.boolean.opBoolean","COPY",EDGE,{"derivedFrom":makeQuery(id+"F9.opExtrude","CAP_EDGE",EDGE,{"disambiguationData":[OSD([sQuery(id+"F6.wireOp",EDGE,"E6.left")])],"isStart":true})});
            var Q15;
            Q15=makeQuery(id+"F9.boolean.opBoolean","COPY",EDGE,{"derivedFrom":makeQuery(id+"F9.opExtrude","CAP_EDGE",EDGE,{"disambiguationData":[OSD([sQuery(id+"F6.wireOp",EDGE,"E5.bottom")])],"isStart":true})});
            var Q16;
            Q16=makeQuery(id+"F9.boolean.opBoolean","COPY",EDGE,{"derivedFrom":makeQuery(id+"F9.opExtrude","CAP_EDGE",EDGE,{"disambiguationData":[OSD([sQuery(id+"F6.wireOp",EDGE,"E5.left")])],"isStart":true})});
            var Q17;
            Q17=makeQuery(id+"F9.boolean.opBoolean","COPY",EDGE,{"derivedFrom":makeQuery(id+"F9.opExtrude","CAP_EDGE",EDGE,{"disambiguationData":[OSD([sQuery(id+"F6.wireOp",EDGE,"E5.top")])],"isStart":true})});
            var Q18;
            Q18=makeQuery(id+"F9.boolean.opBoolean","COPY",EDGE,{"derivedFrom":makeQuery(id+"F9.opExtrude","CAP_EDGE",EDGE,{"disambiguationData":[OSD([sQuery(id+"F6.wireOp",EDGE,"E5.right")])],"isStart":true})});
            var Q19;
            Q19=makeQuery(id+"F9.boolean.opBoolean","COPY",EDGE,{"derivedFrom":makeQuery(id+"F9.opExtrude","CAP_EDGE",EDGE,{"disambiguationData":[OSD([sQuery(id+"F6.wireOp",EDGE,"E4.bottom")])],"isStart":false})});
            var Q20;
            Q20=makeQuery(id+"F9.boolean.opBoolean","COPY",EDGE,{"derivedFrom":makeQuery(id+"F9.opExtrude","CAP_EDGE",EDGE,{"disambiguationData":[OSD([sQuery(id+"F6.wireOp",EDGE,"E2.bottom")])],"isStart":false})});
            var Q21;
            Q21=makeQuery(id+"F9.boolean.opBoolean","COPY",EDGE,{"derivedFrom":makeQuery(id+"F9.opExtrude","CAP_EDGE",EDGE,{"disambiguationData":[OSD([sQuery(id+"F6.wireOp",EDGE,"E6.top")])],"isStart":false})});
            var Q22;
            Q22=makeQuery(id+"F9.boolean.opBoolean","COPY",EDGE,{"derivedFrom":makeQuery(id+"F9.opExtrude","CAP_EDGE",EDGE,{"disambiguationData":[OSD([sQuery(id+"F6.wireOp",EDGE,"E7.top")])],"isStart":false})});
            var Q23;
            Q23=makeQuery(id+"F9.boolean.opBoolean","COPY",EDGE,{"derivedFrom":makeQuery(id+"F9.opExtrude","CAP_EDGE",EDGE,{"disambiguationData":[OSD([sQuery(id+"F6.wireOp",EDGE,"E5.top")])],"isStart":false})});
            var Q24;
            Q24=makeQuery(id+"F9.boolean.opBoolean","COPY",EDGE,{"derivedFrom":makeQuery(id+"F9.opExtrude","SWEPT_EDGE",EDGE,{"disambiguationData":[OSD([sQuery(id+"F6.wireOp",EDGE,"E4.top"),sQuery(id+"F6.wireOp",EDGE,"E4.right")])]})});
            var Q25;
            Q25=makeQuery(id+"F9.boolean.opBoolean","COPY",EDGE,{"derivedFrom":makeQuery(id+"F9.opExtrude","CAP_EDGE",EDGE,{"disambiguationData":[OSD([sQuery(id+"F6.wireOp",EDGE,"E4.top")])],"isStart":false})});
            var Q26;
            Q26=makeQuery(id+"F9.boolean.opBoolean","COPY",EDGE,{"derivedFrom":makeQuery(id+"F9.opExtrude","CAP_EDGE",EDGE,{"disambiguationData":[OSD([sQuery(id+"F6.wireOp",EDGE,"E4.right")])],"isStart":false})});
            var Q27;
            Q27=makeQuery(id+"F9.boolean.opBoolean","COPY",EDGE,{"derivedFrom":makeQuery(id+"F9.opExtrude","CAP_EDGE",EDGE,{"disambiguationData":[OSD([sQuery(id+"F6.wireOp",EDGE,"E6.bottom")])],"isStart":false})});
            var Q28;
            Q28=makeQuery(id+"F9.boolean.opBoolean","COPY",EDGE,{"derivedFrom":makeQuery(id+"F9.opExtrude","CAP_EDGE",EDGE,{"disambiguationData":[OSD([sQuery(id+"F6.wireOp",EDGE,"E6.right")])],"isStart":false})});
            var Q29;
            Q29=makeQuery(id+"F9.boolean.opBoolean","COPY",EDGE,{"derivedFrom":makeQuery(id+"F9.opExtrude","SWEPT_EDGE",EDGE,{"disambiguationData":[OSD([sQuery(id+"F6.wireOp",EDGE,"E6.bottom"),sQuery(id+"F6.wireOp",EDGE,"E6.right")])]})});
            var Q30;
            Q30=makeQuery(id+"F9.boolean.opBoolean","COPY",EDGE,{"derivedFrom":makeQuery(id+"F9.opExtrude","CAP_EDGE",EDGE,{"disambiguationData":[OSD([sQuery(id+"F6.wireOp",EDGE,"E8")])],"isStart":false})});
            var Q31;
            Q31=makeQuery(id+"F9.boolean.opBoolean","COPY",EDGE,{"derivedFrom":makeQuery(id+"F9.opExtrude","SWEPT_EDGE",EDGE,{"disambiguationData":[OSD([sQuery(id+"F6.wireOp",EDGE,"E2.right"),sQuery(id+"F6.wireOp",EDGE,"E8")])]})});
            var Q32;
            Q32=makeQuery(id+"F9.boolean.opBoolean","COPY",EDGE,{"derivedFrom":makeQuery(id+"F9.opExtrude","CAP_EDGE",EDGE,{"disambiguationData":[OSD([sQuery(id+"F6.wireOp",EDGE,"E2.right")])],"isStart":false})});
            var Q33;
            Q33=makeQuery(id+"F9.boolean.opBoolean","COPY",EDGE,{"derivedFrom":makeQuery(id+"F9.opExtrude","CAP_EDGE",EDGE,{"disambiguationData":[OSD([sQuery(id+"F6.wireOp",EDGE,"E7.bottom")])],"isStart":false})});
            var Q34;
            Q34=makeQuery(id+"F9.boolean.opBoolean","COPY",EDGE,{"derivedFrom":makeQuery(id+"F9.opExtrude","SWEPT_EDGE",EDGE,{"disambiguationData":[OSD([sQuery(id+"F6.wireOp",EDGE,"E7.bottom"),sQuery(id+"F6.wireOp",EDGE,"E7.left")])]})});
            var Q35;
            Q35=makeQuery(id+"F9.boolean.opBoolean","COPY",EDGE,{"derivedFrom":makeQuery(id+"F9.opExtrude","CAP_EDGE",EDGE,{"disambiguationData":[OSD([sQuery(id+"F6.wireOp",EDGE,"E7.left")])],"isStart":false})});
            var Q36;
            Q36=makeQuery(id+"F9.boolean.opBoolean","COPY",EDGE,{"derivedFrom":makeQuery(id+"F9.opExtrude","CAP_EDGE",EDGE,{"disambiguationData":[OSD([sQuery(id+"F6.wireOp",EDGE,"E5.bottom")])],"isStart":false})});
            var Q37;
            Q37=makeQuery(id+"F9.boolean.opBoolean","COPY",EDGE,{"derivedFrom":makeQuery(id+"F9.opExtrude","SWEPT_EDGE",EDGE,{"disambiguationData":[OSD([sQuery(id+"F6.wireOp",EDGE,"E5.bottom"),sQuery(id+"F6.wireOp",EDGE,"E5.left")])]})});
            var Q38;
            Q38=makeQuery(id+"F9.boolean.opBoolean","COPY",EDGE,{"derivedFrom":makeQuery(id+"F9.opExtrude","CAP_EDGE",EDGE,{"disambiguationData":[OSD([sQuery(id+"F6.wireOp",EDGE,"E5.left")])],"isStart":false})});
            var Q39;
            Q39=makeQuery(id+"F14.opFillet","BLEND_EDGE",EDGE,{"blendedFrom":[makeQuery(id+"F13.boolean.opBoolean","COPY",EDGE,{"derivedFrom":makeQuery(id+"F13.opExtrude","CAP_EDGE",EDGE,{"disambiguationData":[OSD([sQuery(id+"F12.wireOp",EDGE,"E18")])],"isStart":false})}),makeQuery(id+"F5.opExtrude","SWEPT_FACE",FACE,{"disambiguationData":[OSD([sQuery(id+"F4.wireOp",EDGE,"E1")])]})],"blendedInto":[makeQuery(id+"F5.opExtrude","SWEPT_FACE",FACE,{"disambiguationData":[OSD([sQuery(id+"F4.wireOp",EDGE,"E1")])]})]});
            var Q40;
            Q40=makeQuery(id+"F5.opExtrude","CAP_EDGE",EDGE,{"disambiguationData":[OSD([sQuery(id+"F4.wireOp",EDGE,"E1")])],"isStart":true});
            var Q41;
            {var subQ0=sQuery(id+"F10.wireOp",EDGE,"E12");Q41=makeQuery(id+"F15.opFillet","BLEND_EDGE",EDGE,{"blendedFrom":[makeQuery(id+"F11.boolean.opBoolean","COPY",EDGE,{"derivedFrom":makeQuery(id+"F11.opExtrude","CAP_EDGE",EDGE,{"disambiguationData":[OSD([subQ0])],"isStart":false})}),makeQuery(id+"F11.boolean.opBoolean","COPY",FACE,{"derivedFrom":makeQuery(id+"F11.opExtrude","CAP_FACE",FACE,{"disambiguationData":[OSD([subQ0,sQuery(id+"F10.wireOp",EDGE,"E13.bottom"),sQuery(id+"F10.wireOp",EDGE,"E13.top"),sQuery(id+"F10.wireOp",EDGE,"E13.left"),sQuery(id+"F10.wireOp",EDGE,"E13.right"),sQuery(id+"F10.wireOp",EDGE,"E14.bottom"),sQuery(id+"F10.wireOp",EDGE,"E14.top"),sQuery(id+"F10.wireOp",EDGE,"E14.left"),sQuery(id+"F10.wireOp",EDGE,"E14.right"),sQuery(id+"F10.wireOp",EDGE,"E15.bottom"),sQuery(id+"F10.wireOp",EDGE,"E15.top"),sQuery(id+"F10.wireOp",EDGE,"E15.left"),sQuery(id+"F10.wireOp",EDGE,"E15.right"),sQuery(id+"F10.wireOp",EDGE,"E16.bottom"),sQuery(id+"F10.wireOp",EDGE,"E16.top"),sQuery(id+"F10.wireOp",EDGE,"E16.left"),sQuery(id+"F10.wireOp",EDGE,"E16.right"),sQuery(id+"F10.wireOp",EDGE,"E17.bottom"),sQuery(id+"F10.wireOp",EDGE,"E17.top"),sQuery(id+"F10.wireOp",EDGE,"E17.left"),sQuery(id+"F10.wireOp",EDGE,"E17.right")])],"isStart":false})})],"blendedInto":[makeQuery(id+"F11.boolean.opBoolean","COPY",FACE,{"derivedFrom":makeQuery(id+"F11.opExtrude","CAP_FACE",FACE,{"disambiguationData":[OSD([subQ0,sQuery(id+"F10.wireOp",EDGE,"E13.bottom"),sQuery(id+"F10.wireOp",EDGE,"E13.top"),sQuery(id+"F10.wireOp",EDGE,"E13.left"),sQuery(id+"F10.wireOp",EDGE,"E13.right"),sQuery(id+"F10.wireOp",EDGE,"E14.bottom"),sQuery(id+"F10.wireOp",EDGE,"E14.top"),sQuery(id+"F10.wireOp",EDGE,"E14.left"),sQuery(id+"F10.wireOp",EDGE,"E14.right"),sQuery(id+"F10.wireOp",EDGE,"E15.bottom"),sQuery(id+"F10.wireOp",EDGE,"E15.top"),sQuery(id+"F10.wireOp",EDGE,"E15.left"),sQuery(id+"F10.wireOp",EDGE,"E15.right"),sQuery(id+"F10.wireOp",EDGE,"E16.bottom"),sQuery(id+"F10.wireOp",EDGE,"E16.top"),sQuery(id+"F10.wireOp",EDGE,"E16.left"),sQuery(id+"F10.wireOp",EDGE,"E16.right"),sQuery(id+"F10.wireOp",EDGE,"E17.bottom"),sQuery(id+"F10.wireOp",EDGE,"E17.top"),sQuery(id+"F10.wireOp",EDGE,"E17.left"),sQuery(id+"F10.wireOp",EDGE,"E17.right")])],"isStart":false})})]});}
            var Q42;
            {var subQ0=sQuery(id+"F10.wireOp",EDGE,"E12");Q42=makeQuery(id+"F15.opFillet","BLEND_EDGE",EDGE,{"blendedFrom":[makeQuery(id+"F11.boolean.opBoolean","COPY",EDGE,{"derivedFrom":makeQuery(id+"F11.opExtrude","CAP_EDGE",EDGE,{"disambiguationData":[OSD([subQ0])],"isStart":false})}),makeQuery(id+"F11.boolean.opBoolean","COPY",FACE,{"derivedFrom":makeQuery(id+"F11.opExtrude","SWEPT_FACE",FACE,{"disambiguationData":[OSD([subQ0])]})})],"blendedInto":[makeQuery(id+"F11.boolean.opBoolean","COPY",FACE,{"derivedFrom":makeQuery(id+"F11.opExtrude","SWEPT_FACE",FACE,{"disambiguationData":[OSD([subQ0])]})})]});}
            var Q43;
            Q43=makeQuery(id+"F9.boolean.opBoolean","COPY",EDGE,{"derivedFrom":makeQuery(id+"F9.opExtrude","SWEPT_EDGE",EDGE,{"disambiguationData":[OSD([sQuery(id+"F6.wireOp",EDGE,"E6.bottom"),sQuery(id+"F6.wireOp",EDGE,"E6.left")])]})});
            var Q44;
            Q44=makeQuery(id+"F9.boolean.opBoolean","COPY",EDGE,{"derivedFrom":makeQuery(id+"F9.opExtrude","SWEPT_EDGE",EDGE,{"disambiguationData":[OSD([sQuery(id+"F6.wireOp",EDGE,"E2.left"),sQuery(id+"F6.wireOp",EDGE,"E8")])]})});
            var Q45;
            Q45=makeQuery(id+"F9.boolean.opBoolean","COPY",EDGE,{"derivedFrom":makeQuery(id+"F9.opExtrude","SWEPT_EDGE",EDGE,{"disambiguationData":[OSD([sQuery(id+"F6.wireOp",EDGE,"E7.bottom"),sQuery(id+"F6.wireOp",EDGE,"E7.right")])]})});
            var Q46;
            Q46=makeQuery(id+"F9.boolean.opBoolean","COPY",EDGE,{"derivedFrom":makeQuery(id+"F9.opExtrude","SWEPT_EDGE",EDGE,{"disambiguationData":[OSD([sQuery(id+"F6.wireOp",EDGE,"E5.bottom"),sQuery(id+"F6.wireOp",EDGE,"E5.right")])]})});
            var Q47;
            Q47=makeQuery(id+"F9.boolean.opBoolean","COPY",EDGE,{"derivedFrom":makeQuery(id+"F9.opExtrude","SWEPT_EDGE",EDGE,{"disambiguationData":[OSD([sQuery(id+"F6.wireOp",EDGE,"E4.top"),sQuery(id+"F6.wireOp",EDGE,"E4.left")])]})});
            var Q48;
            Q48=makeQuery(id+"F9.boolean.opBoolean","COPY",EDGE,{"derivedFrom":makeQuery(id+"F9.opExtrude","CAP_EDGE",EDGE,{"disambiguationData":[OSD([sQuery(id+"F6.wireOp",EDGE,"E4.left")])],"isStart":false})});
            var Q49;
            Q49=makeQuery(id+"F9.boolean.opBoolean","COPY",EDGE,{"derivedFrom":makeQuery(id+"F9.opExtrude","CAP_EDGE",EDGE,{"disambiguationData":[OSD([sQuery(id+"F6.wireOp",EDGE,"E2.left")])],"isStart":false})});
            var Q50;
            Q50=makeQuery(id+"F9.boolean.opBoolean","COPY",EDGE,{"derivedFrom":makeQuery(id+"F9.opExtrude","CAP_EDGE",EDGE,{"disambiguationData":[OSD([sQuery(id+"F6.wireOp",EDGE,"E6.left")])],"isStart":false})});
            var Q51;
            Q51=makeQuery(id+"F9.boolean.opBoolean","COPY",EDGE,{"derivedFrom":makeQuery(id+"F9.opExtrude","CAP_EDGE",EDGE,{"disambiguationData":[OSD([sQuery(id+"F6.wireOp",EDGE,"E7.right")])],"isStart":false})});
            var Q52;
            Q52=makeQuery(id+"F9.boolean.opBoolean","COPY",EDGE,{"derivedFrom":makeQuery(id+"F9.opExtrude","CAP_EDGE",EDGE,{"disambiguationData":[OSD([sQuery(id+"F6.wireOp",EDGE,"E5.right")])],"isStart":false})});
            var Q53;
            Q53=makeQuery(id+"F9.boolean.opBoolean","COPY",EDGE,{"derivedFrom":makeQuery(id+"F9.opExtrude","SWEPT_EDGE",EDGE,{"disambiguationData":[OSD([sQuery(id+"F6.wireOp",EDGE,"E2.bottom"),sQuery(id+"F6.wireOp",EDGE,"E2.right")])]})});
            var Q54;
            Q54=makeQuery(id+"F9.boolean.opBoolean","COPY",EDGE,{"derivedFrom":makeQuery(id+"F9.opExtrude","SWEPT_EDGE",EDGE,{"disambiguationData":[OSD([sQuery(id+"F6.wireOp",EDGE,"E4.bottom"),sQuery(id+"F6.wireOp",EDGE,"E4.right")])]})});
            var Q55;
            Q55=makeQuery(id+"F9.boolean.opBoolean","COPY",EDGE,{"derivedFrom":makeQuery(id+"F9.opExtrude","SWEPT_EDGE",EDGE,{"disambiguationData":[OSD([sQuery(id+"F6.wireOp",EDGE,"E6.top"),sQuery(id+"F6.wireOp",EDGE,"E6.right")])]})});
            var Q56;
            Q56=makeQuery(id+"F9.boolean.opBoolean","COPY",EDGE,{"derivedFrom":makeQuery(id+"F9.opExtrude","SWEPT_EDGE",EDGE,{"disambiguationData":[OSD([sQuery(id+"F6.wireOp",EDGE,"E7.top"),sQuery(id+"F6.wireOp",EDGE,"E7.left")])]})});
            var Q57;
            Q57=makeQuery(id+"F9.boolean.opBoolean","COPY",EDGE,{"derivedFrom":makeQuery(id+"F9.opExtrude","SWEPT_EDGE",EDGE,{"disambiguationData":[OSD([sQuery(id+"F6.wireOp",EDGE,"E5.top"),sQuery(id+"F6.wireOp",EDGE,"E5.left")])]})});
            var Q58;
            Q58=makeQuery(id+"F9.boolean.opBoolean","COPY",EDGE,{"derivedFrom":makeQuery(id+"F9.opExtrude","SWEPT_EDGE",EDGE,{"disambiguationData":[OSD([sQuery(id+"F6.wireOp",EDGE,"E4.bottom"),sQuery(id+"F6.wireOp",EDGE,"E4.left")])]})});
            var Q59;
            Q59=makeQuery(id+"F9.boolean.opBoolean","COPY",EDGE,{"derivedFrom":makeQuery(id+"F9.opExtrude","SWEPT_EDGE",EDGE,{"disambiguationData":[OSD([sQuery(id+"F6.wireOp",EDGE,"E6.top"),sQuery(id+"F6.wireOp",EDGE,"E6.left")])]})});
            var Q60;
            Q60=makeQuery(id+"F9.boolean.opBoolean","COPY",EDGE,{"derivedFrom":makeQuery(id+"F9.opExtrude","SWEPT_EDGE",EDGE,{"disambiguationData":[OSD([sQuery(id+"F6.wireOp",EDGE,"E2.bottom"),sQuery(id+"F6.wireOp",EDGE,"E2.left")])]})});
            var Q61;
            Q61=makeQuery(id+"F9.boolean.opBoolean","COPY",EDGE,{"derivedFrom":makeQuery(id+"F9.opExtrude","SWEPT_EDGE",EDGE,{"disambiguationData":[OSD([sQuery(id+"F6.wireOp",EDGE,"E7.top"),sQuery(id+"F6.wireOp",EDGE,"E7.right")])]})});
            var Q62;
            Q62=makeQuery(id+"F9.boolean.opBoolean","COPY",EDGE,{"derivedFrom":makeQuery(id+"F9.opExtrude","SWEPT_EDGE",EDGE,{"disambiguationData":[OSD([sQuery(id+"F6.wireOp",EDGE,"E5.top"),sQuery(id+"F6.wireOp",EDGE,"E5.right")])]})});
            fillet(context, id + "F16", {"entities" : qUnion([Q0, Q1, Q2, Q3, Q4, Q5, Q6, Q7, Q8, Q9, Q10, Q11, Q12, Q13, Q14, Q15, Q16, Q17, Q18, Q19, Q20, Q21, Q22, Q23, Q24, Q25, Q26, Q27, Q28, Q29, Q30, Q31, Q32, Q33, Q34, Q35, Q36, Q37, Q38, Q39, Q40, Q41, Q42, Q43, Q44, Q45, Q46, Q47, Q48, Q49, Q50, Q51, Q52, Q53, Q54, Q55, Q56, Q57, Q58, Q59, Q60, Q61, Q62]), "radius" : 1 * mm, "tangentPropagation" : true, "allowEdgeOverflow" : false});
        }
        {
            var Q0;
            Q0=qCreatedBy(makeId("Top.planeOp"),FACE);
            var sketch = newSketch(context, id + "F17", { "sketchPlane" : qUnion([Q0])});
            skCircle(sketch, "E20", {"center": v(69.37, -77.22) * mm, "radius": 45 * mm});
            skArc(sketch, "E21", {"start": v(113.26, -87.15) * mm, "mid": v(124.37, -77.22) * mm, "end": v(113.26, -67.28) * mm});
            skSolve(sketch);
        }
        {
            var Q0;
            Q0 = qSketchRegion(id + "F17", true);
            extrude(context, id + "F18", {"entities" : qUnion([Q0]), "depth" : 0.1 * mm, "offsetDistance" : 25 * mm});
        }
    });
